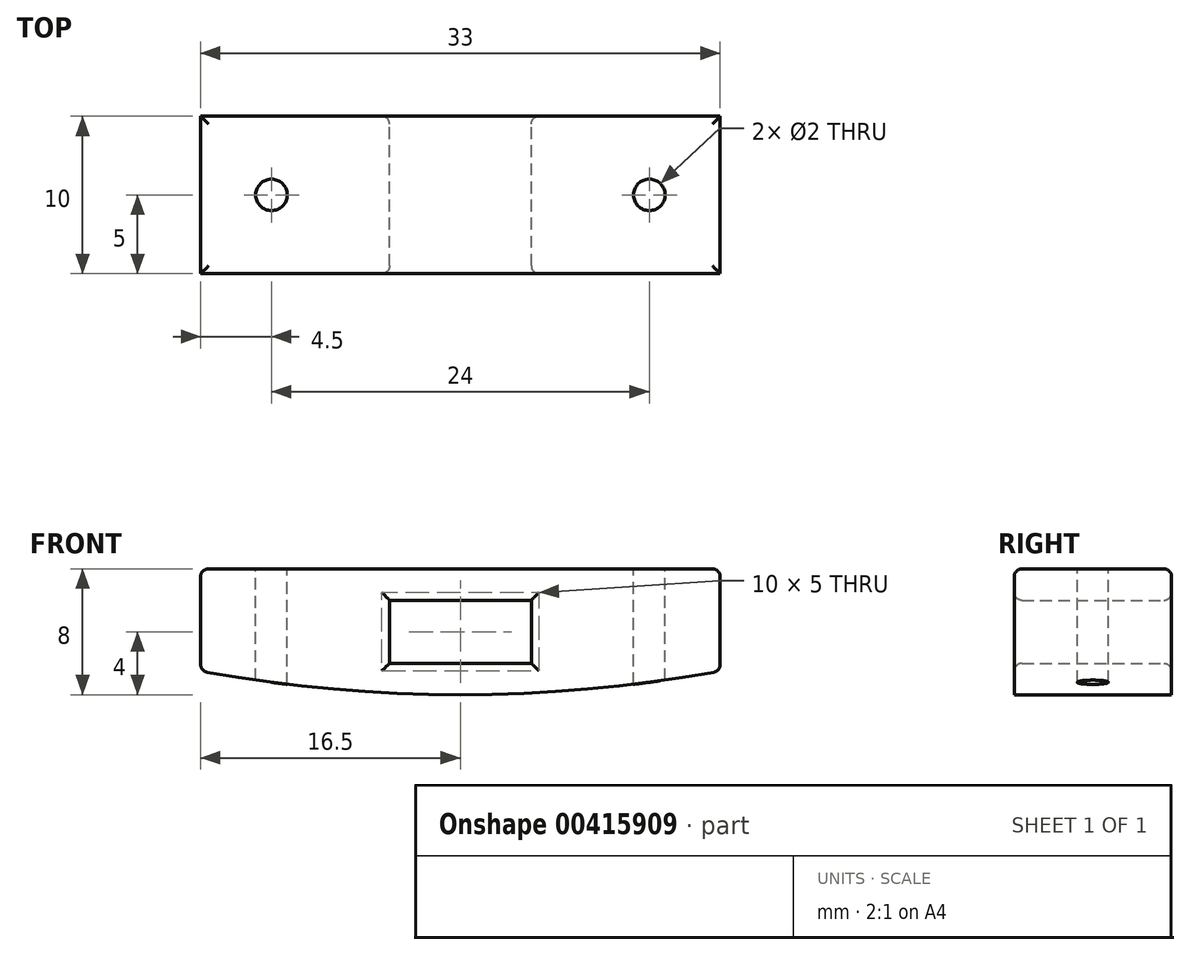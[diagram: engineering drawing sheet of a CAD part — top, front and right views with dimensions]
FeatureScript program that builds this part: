
annotation { "Feature Type Name" : "Feature", "Feature Type Description" : "" }
export const myFeature = defineFeature(function(context is Context, id is Id, definition is map)
    precondition{}
    {
        {
            var Q0;
            Q0=qCreatedBy(makeId("Front.planeOp"),FACE);
            var sketch = newSketch(context, id + "F0", { "sketchPlane" : qUnion([Q0])});
            skLineSegment(sketch, "E0.bottom", {"start": v(4.5, -2) * mm, "end": v(-4.5, -2) * mm});
            skLineSegment(sketch, "E0.top", {"start": v(4.5, 2) * mm, "end": v(-4.5, 2) * mm});
            skLineSegment(sketch, "E0.left", {"start": v(4.5, -2) * mm, "end": v(4.5, 2) * mm});
            skLineSegment(sketch, "E0.right", {"start": v(-4.5, -2) * mm, "end": v(-4.5, 2) * mm});
            skPoint(sketch, "E0.middle", {"position": v(0, 0) * mm});
            skLineSegment(sketch, "E1.bottom", {"start": v(7.5, -4) * mm, "end": v(-7.5, -4) * mm});
            skLineSegment(sketch, "E1.top", {"start": v(7.5, 4) * mm, "end": v(-7.5, 4) * mm});
            skLineSegment(sketch, "E1.left", {"start": v(7.5, -4) * mm, "end": v(7.5, 4) * mm});
            skLineSegment(sketch, "E1.right", {"start": v(-7.5, -4) * mm, "end": v(-7.5, 4) * mm});
            skLineSegment(sketch, "E2.bottom", {"start": v(16.5, 4) * mm, "end": v(-16.5, 4) * mm});
            skLineSegment(sketch, "E2.top", {"start": v(16.5, -4) * mm, "end": v(-16.5, -4) * mm});
            skLineSegment(sketch, "E2.left", {"start": v(16.5, 4) * mm, "end": v(16.5, -4) * mm});
            skLineSegment(sketch, "E2.right", {"start": v(-16.5, 4) * mm, "end": v(-16.5, -4) * mm});
            skLineSegment(sketch, "E3", {"start": v(16.5, -2.5) * mm, "end": v(-16.5, -2.5) * mm});
            skLineSegment(sketch, "E4", {"start": v(0, -2.5) * mm, "end": v(0, -4) * mm});
            skArc(sketch, "E5", {"start": v(-16.5, -2.5) * mm, "mid": v(0, -4) * mm, "end": v(16.5, -2.5) * mm});
            skSolve(sketch);
        }
        {
            var Q0;
            {var subQ0=sQuery(id+"F0.wireOp",EDGE,"E1.left");Q0=makeQuery(id+"F0.imprint","IMPRINT",FACE,{"disambiguationData":[TD([[makeQuery(id+"F0.imprint","IMPRINT",EDGE,{"derivedFrom":subQ0}),-1.0]])]});}
            var Q1;
            Q1=makeQuery(id+"F0.imprint","IMPRINT",FACE,{"disambiguationData":[TD([[makeQuery(id+"F0.imprint","IMPRINT",EDGE,{"derivedFrom":sQuery(id+"F0.wireOp",EDGE,"E0.bottom")}),1.0]])]});
            var Q2;
            {var subQ0=sQuery(id+"F0.wireOp",EDGE,"E1.right");Q2=makeQuery(id+"F0.imprint","IMPRINT",FACE,{"disambiguationData":[TD([[makeQuery(id+"F0.imprint","IMPRINT",EDGE,{"derivedFrom":subQ0}),1.0]])]});}
            var Q3;
            {var subQ5=sQuery(id+"F0.wireOp",EDGE,"E4");Q3=makeQuery(id+"F0.imprint","IMPRINT",FACE,{"disambiguationData":[TD([[makeQuery(id+"F0.imprint","IMPRINT",EDGE,{"derivedFrom":subQ5}),-1.0]])]});}
            var Q4;
            {var subQ5=sQuery(id+"F0.wireOp",EDGE,"E4");Q4=makeQuery(id+"F0.imprint","IMPRINT",FACE,{"disambiguationData":[TD([[makeQuery(id+"F0.imprint","IMPRINT",EDGE,{"derivedFrom":subQ5}),1.0]])]});}
            var Q5;
            {var subQ0=sQuery(id+"F0.wireOp",EDGE,"E2.bottom");var subQ1=sQuery(id+"F0.wireOp",EDGE,"E1.left");var subQ2=makeQuery(id+"F0.imprint","INTERSECT",VERTEX,{"derivedFrom":[subQ1,subQ0]});Q5=makeQuery(id+"F0.imprint","IMPRINT",FACE,{"disambiguationData":[TD([[makeQuery(id+"F0.imprint","IMPRINT",EDGE,{"disambiguationData":[TD([[subQ2,1.0]])],"derivedFrom":subQ1}),-1.0]])]});}
            var Q6;
            {var subQ0=sQuery(id+"F0.wireOp",EDGE,"E2.bottom");var subQ1=sQuery(id+"F0.wireOp",EDGE,"E1.right");var subQ2=makeQuery(id+"F0.imprint","INTERSECT",VERTEX,{"derivedFrom":[subQ1,subQ0]});Q6=makeQuery(id+"F0.imprint","IMPRINT",FACE,{"disambiguationData":[TD([[makeQuery(id+"F0.imprint","IMPRINT",EDGE,{"disambiguationData":[TD([[subQ2,1.0]])],"derivedFrom":subQ1}),1.0]])]});}
            extrude(context, id + "F1", {"entities" : qUnion([Q0, Q1, Q2, Q3, Q4, Q5, Q6]), "depth" : 10 * mm});
        }
        {
            var Q0;
            Q0=makeQuery(id+"F1.opExtrude","SWEPT_EDGE",EDGE,{"disambiguationData":[OSD([sQuery(id+"F0.wireOp",EDGE,"E2.bottom"),sQuery(id+"F0.wireOp",EDGE,"E2.left")])]});
            var Q1;
            Q1=makeQuery(id+"F1.opExtrude","SWEPT_EDGE",EDGE,{"disambiguationData":[OSD([sQuery(id+"F0.wireOp",EDGE,"E2.bottom"),sQuery(id+"F0.wireOp",EDGE,"E2.right")])]});
            var Q2;
            Q2=makeQuery(id+"F1.opExtrude","CAP_EDGE",EDGE,{"disambiguationData":[OSD([sQuery(id+"F0.wireOp",EDGE,"E2.bottom")])],"isStart":false});
            var Q3;
            Q3=makeQuery(id+"F1.opExtrude","CAP_EDGE",EDGE,{"disambiguationData":[OSD([sQuery(id+"F0.wireOp",EDGE,"E2.bottom")])],"isStart":true});
            var Q4;
            Q4=makeQuery(id+"F1.opExtrude","SWEPT_EDGE",EDGE,{"disambiguationData":[OSD([sQuery(id+"F0.wireOp",EDGE,"E2.left"),sQuery(id+"F0.wireOp",EDGE,"E3"),sQuery(id+"F0.wireOp",EDGE,"E5")])]});
            var Q5;
            Q5=makeQuery(id+"F1.opExtrude","SWEPT_EDGE",EDGE,{"disambiguationData":[OSD([sQuery(id+"F0.wireOp",EDGE,"E2.right"),sQuery(id+"F0.wireOp",EDGE,"E3"),sQuery(id+"F0.wireOp",EDGE,"E5")])]});
            var Q6;
            Q6=makeQuery(id+"F1.opExtrude","CAP_EDGE",EDGE,{"disambiguationData":[OSD([sQuery(id+"F0.wireOp",EDGE,"E0.right")])],"isStart":true});
            var Q7;
            Q7=makeQuery(id+"F1.opExtrude","CAP_EDGE",EDGE,{"disambiguationData":[OSD([sQuery(id+"F0.wireOp",EDGE,"E0.top")])],"isStart":true});
            var Q8;
            Q8=makeQuery(id+"F1.opExtrude","CAP_EDGE",EDGE,{"disambiguationData":[OSD([sQuery(id+"F0.wireOp",EDGE,"E0.left")])],"isStart":true});
            var Q9;
            Q9=makeQuery(id+"F1.opExtrude","CAP_EDGE",EDGE,{"disambiguationData":[OSD([sQuery(id+"F0.wireOp",EDGE,"E0.bottom")])],"isStart":true});
            var Q10;
            Q10=makeQuery(id+"F1.opExtrude","CAP_EDGE",EDGE,{"disambiguationData":[OSD([sQuery(id+"F0.wireOp",EDGE,"E0.right")])],"isStart":false});
            var Q11;
            Q11=makeQuery(id+"F1.opExtrude","CAP_EDGE",EDGE,{"disambiguationData":[OSD([sQuery(id+"F0.wireOp",EDGE,"E0.top")])],"isStart":false});
            var Q12;
            Q12=makeQuery(id+"F1.opExtrude","CAP_EDGE",EDGE,{"disambiguationData":[OSD([sQuery(id+"F0.wireOp",EDGE,"E0.left")])],"isStart":false});
            var Q13;
            Q13=makeQuery(id+"F1.opExtrude","CAP_EDGE",EDGE,{"disambiguationData":[OSD([sQuery(id+"F0.wireOp",EDGE,"E0.bottom")])],"isStart":false});
            fillet(context, id + "F2", {"entities" : qUnion([Q0, Q1, Q2, Q3, Q4, Q5, Q6, Q7, Q8, Q9, Q10, Q11, Q12, Q13]), "radius" : .5 * mm, "tangentPropagation" : true, "allowEdgeOverflow" : false});
        }
        {
            var Q0;
            Q0=makeQuery(id+"F1.opExtrude","SWEPT_FACE",FACE,{"disambiguationData":[OSD([sQuery(id+"F0.wireOp",EDGE,"E2.bottom")])]});
            var sketch = newSketch(context, id + "F3", { "sketchPlane" : qUnion([Q0])});
            skCircle(sketch, "E6", {"center": v(-12, -5) * mm, "radius": 1 * mm});
            skCircle(sketch, "E7", {"center": v(12, -5) * mm, "radius": 1 * mm});
            skSolve(sketch);
        }
        {
            var Q0;
            Q0=makeQuery(id+"F3.imprint","IMPRINT",FACE,{"disambiguationData":[TD([[makeQuery(id+"F3.imprint","IMPRINT",EDGE,{"derivedFrom":sQuery(id+"F3.wireOp",EDGE,"E6")}),1.0]])]});
            var Q1;
            Q1=makeQuery(id+"F3.imprint","IMPRINT",FACE,{"disambiguationData":[TD([[makeQuery(id+"F3.imprint","IMPRINT",EDGE,{"derivedFrom":sQuery(id+"F3.wireOp",EDGE,"E7")}),1.0]])]});
            extrude(context, id + "F4", {"entities" : qUnion([Q0, Q1]), "operationType" : NewBodyOperationType.REMOVE, "oppositeDirection" : true, "depth" : 25 * mm});
        }
    });
